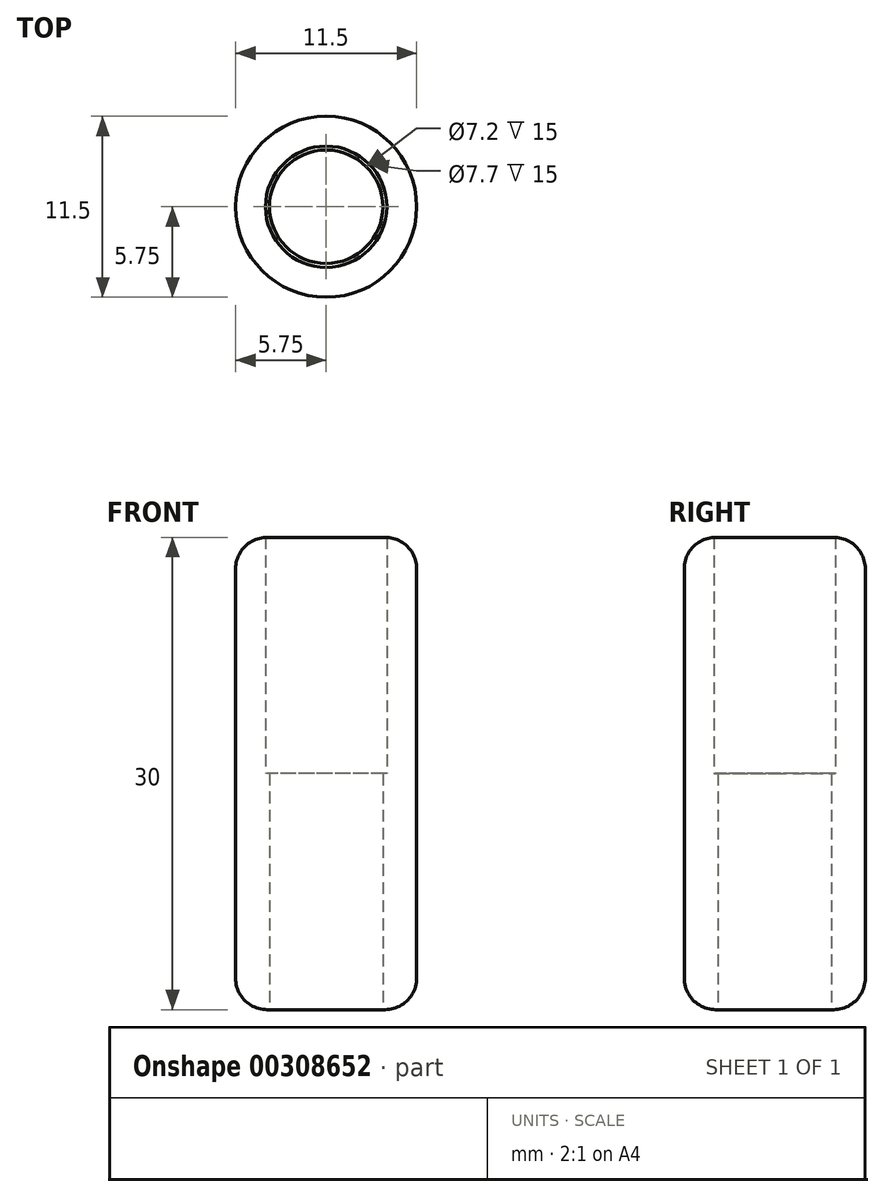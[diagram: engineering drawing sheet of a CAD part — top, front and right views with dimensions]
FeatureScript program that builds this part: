
annotation { "Feature Type Name" : "Feature", "Feature Type Description" : "" }
export const myFeature = defineFeature(function(context is Context, id is Id, definition is map)
    precondition{}
    {
        {
            var Q0;
            Q0=qCreatedBy(makeId("Top.planeOp"),FACE);
            var sketch = newSketch(context, id + "F0", { "sketchPlane" : qUnion([Q0])});
            skCircle(sketch, "E0", {"center": v(0, 0) * mm, "radius": 3.6 * mm});
            skCircle(sketch, "E1", {"center": v(0, 0) * mm, "radius": 3.85 * mm});
            skCircle(sketch, "E2", {"center": v(0, 0) * mm, "radius": 5.75 * mm});
            skSolve(sketch);
        }
        {
            var Q0;
            Q0=makeQuery(id+"F0.imprint","IMPRINT",FACE,{"disambiguationData":[TD([[makeQuery(id+"F0.imprint","IMPRINT",EDGE,{"derivedFrom":sQuery(id+"F0.wireOp",EDGE,"E0")}),-1.0]])]});
            var Q1;
            Q1=makeQuery(id+"F0.imprint","IMPRINT",FACE,{"disambiguationData":[TD([[makeQuery(id+"F0.imprint","IMPRINT",EDGE,{"derivedFrom":sQuery(id+"F0.wireOp",EDGE,"u9wZAYXc-DP7u-milv-G3LX-5S4ReEsq80q7")}),1.0]])]});
            var Q2;
            Q2=makeQuery(id+"F0.imprint","IMPRINT",FACE,{"disambiguationData":[TD([[makeQuery(id+"F0.imprint","IMPRINT",EDGE,{"derivedFrom":sQuery(id+"F0.wireOp",EDGE,"E0")}),1.0]])]});
            var Q3;
            Q3=makeQuery(id+"F0.imprint","IMPRINT",FACE,{"disambiguationData":[TD([[makeQuery(id+"F0.imprint","IMPRINT",EDGE,{"derivedFrom":sQuery(id+"F0.wireOp",EDGE,"E1")}),-1.0]])]});
            extrude(context, id + "F1", {"entities" : qUnion([Q0, Q1, Q2, Q3]), "depth" : 30 * mm});
        }
        {
            var Q0;
            Q0=makeQuery(id+"F0.imprint","IMPRINT",FACE,{"disambiguationData":[TD([[makeQuery(id+"F0.imprint","IMPRINT",EDGE,{"derivedFrom":sQuery(id+"F0.wireOp",EDGE,"E0")}),1.0]])]});
            extrude(context, id + "F2", {"entities" : qUnion([Q0]), "operationType" : NewBodyOperationType.REMOVE, "depth" : 15 * mm});
        }
        {
            var Q0;
            Q0=makeQuery(id+"F0.imprint","IMPRINT",FACE,{"disambiguationData":[TD([[makeQuery(id+"F0.imprint","IMPRINT",EDGE,{"derivedFrom":sQuery(id+"F0.wireOp",EDGE,"E0")}),1.0]])]});
            var Q1;
            Q1=makeQuery(id+"F0.imprint","IMPRINT",FACE,{"disambiguationData":[TD([[makeQuery(id+"F0.imprint","IMPRINT",EDGE,{"derivedFrom":sQuery(id+"F0.wireOp",EDGE,"E0")}),-1.0]])]});
            extrude(context, id + "F3", {"entities" : qUnion([Q0, Q1]), "operationType" : NewBodyOperationType.REMOVE, "depth" : 30 * mm, "hasSecondDirection" : true, "secondDirectionOppositeDirection" : false, "secondDirectionDepth" : 15 * mm});
        }
        {
            var Q0;
            Q0=makeQuery(id+"F1.opExtrude","CAP_EDGE",EDGE,{"disambiguationData":[OSD([sQuery(id+"F0.wireOp",EDGE,"E2")])],"isStart":false});
            var Q1;
            Q1=makeQuery(id+"F1.opExtrude","CAP_EDGE",EDGE,{"disambiguationData":[OSD([sQuery(id+"F0.wireOp",EDGE,"E2")])],"isStart":true});
            fillet(context, id + "F4", {"entities" : qUnion([Q0, Q1]), "radius" : 2 * mm, "tangentPropagation" : true, "allowEdgeOverflow" : false});
        }
    });
